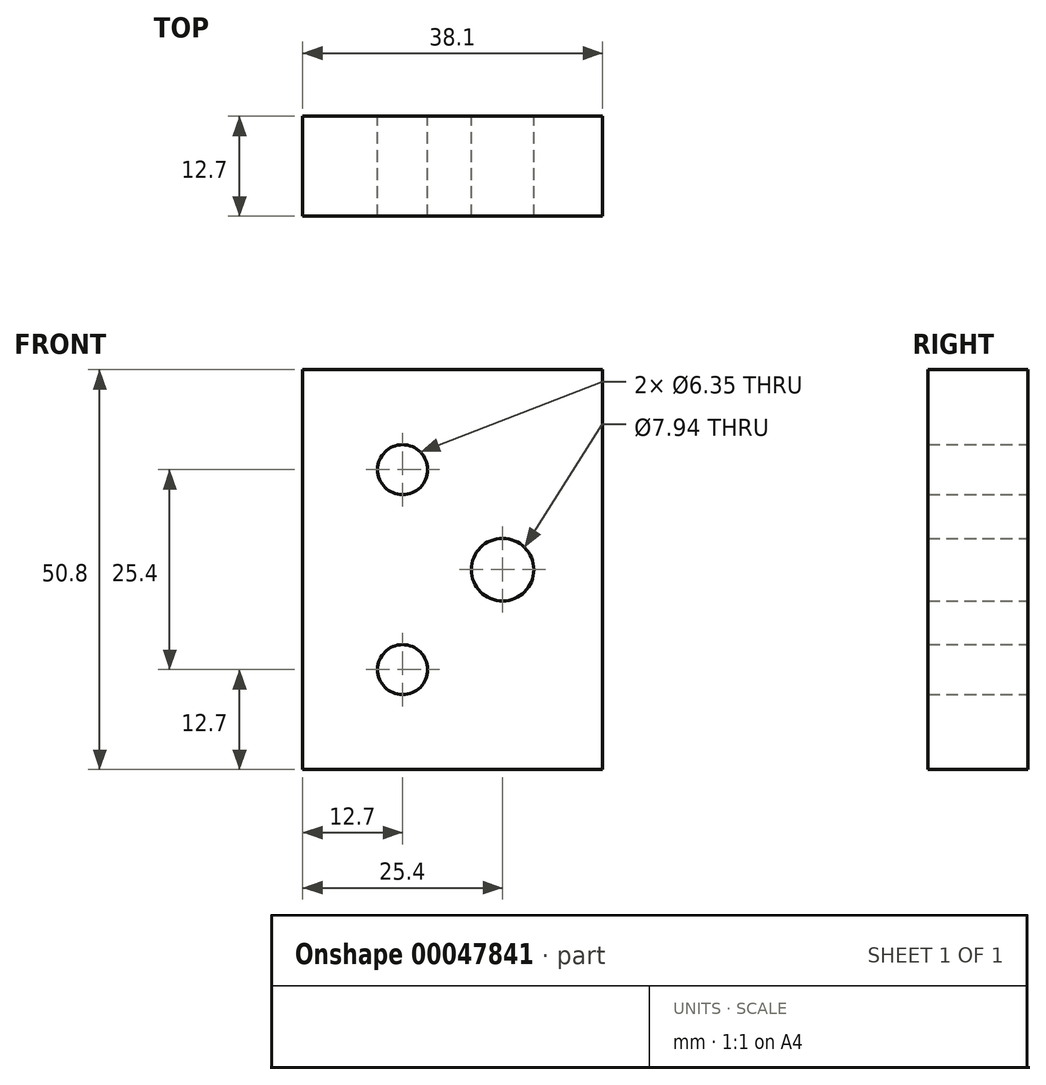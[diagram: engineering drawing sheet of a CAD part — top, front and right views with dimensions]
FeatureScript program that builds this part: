
annotation { "Feature Type Name" : "Feature", "Feature Type Description" : "" }
export const myFeature = defineFeature(function(context is Context, id is Id, definition is map)
    precondition{}
    {
        {
            var Q0;
            Q0=qCreatedBy(makeId("Front.planeOp"),FACE);
            var sketch = newSketch(context, id + "F0", { "sketchPlane" : qUnion([Q0])});
            skLineSegment(sketch, "E0.bottom", {"start": v(0, 50.8) * mm, "end": v(38.1, 50.8) * mm});
            skLineSegment(sketch, "E0.top", {"start": v(0, 0) * mm, "end": v(38.1, 0) * mm});
            skLineSegment(sketch, "E0.left", {"start": v(0, 50.8) * mm, "end": v(0, 0) * mm});
            skLineSegment(sketch, "E0.right", {"start": v(38.1, 50.8) * mm, "end": v(38.1, 0) * mm});
            skCircle(sketch, "E1", {"center": v(12.7, 38.1) * mm, "radius": 3.18 * mm});
            skCircle(sketch, "E2", {"center": v(12.7, 12.7) * mm, "radius": 3.18 * mm});
            skCircle(sketch, "E3", {"center": v(25.4, 25.4) * mm, "radius": 3.97 * mm});
            skSolve(sketch);
        }
        {
            var Q0;
            Q0=makeQuery(id+"F0.imprint","IMPRINT",FACE,{"disambiguationData":[TD([[makeQuery(id+"F0.imprint","IMPRINT",EDGE,{"derivedFrom":sQuery(id+"F0.wireOp",EDGE,"E0.bottom")}),-1.0]])]});
            extrude(context, id + "F1", {"entities" : qUnion([Q0]), "depth" : 12.7 * mm});
        }
    });
